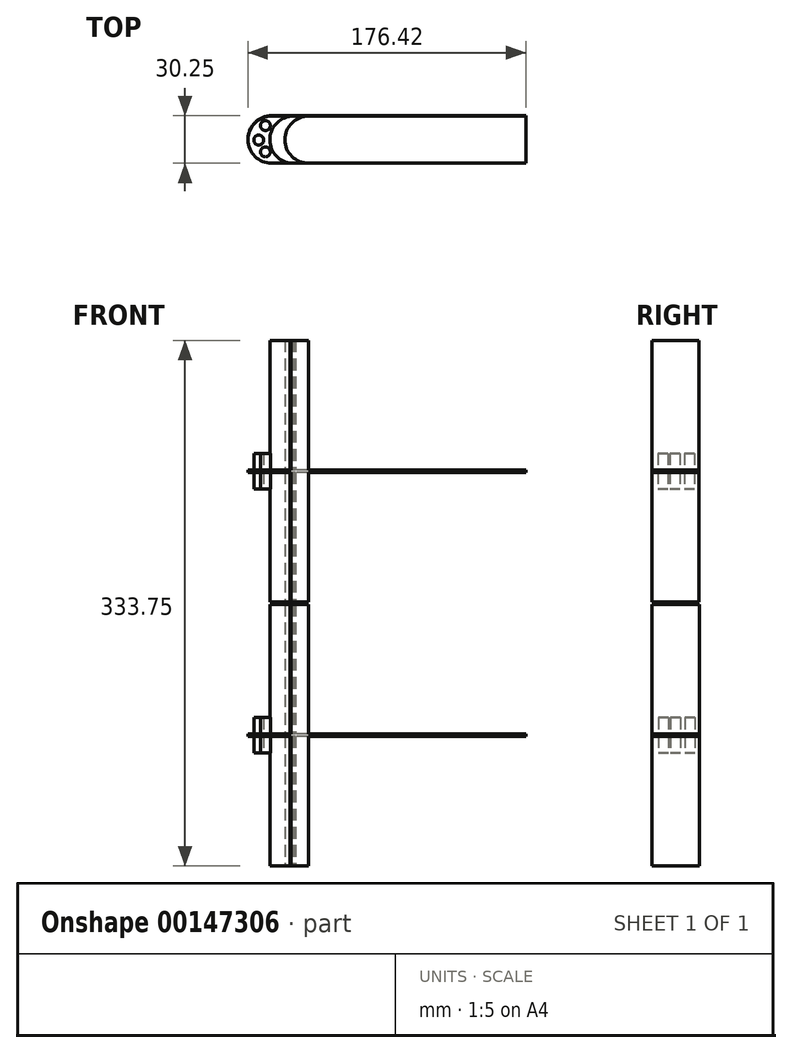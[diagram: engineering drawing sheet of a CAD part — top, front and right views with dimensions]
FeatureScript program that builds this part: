
annotation { "Feature Type Name" : "Feature", "Feature Type Description" : "" }
export const myFeature = defineFeature(function(context is Context, id is Id, definition is map)
    precondition{}
    {
        {
            var Q0;
            Q0=qCreatedBy(makeId("Top.planeOp"),FACE);
            var sketch = newSketch(context, id + "F0", { "sketchPlane" : qUnion([Q0])});
            skLineSegment(sketch, "E0.bottom", {"start": v(53.72, 4.42) * mm, "end": v(-107.7, 4.42) * mm});
            skLineSegment(sketch, "E0.top", {"start": v(53.72, 34.42) * mm, "end": v(-107.7, 34.42) * mm});
            skLineSegment(sketch, "E0.left", {"start": v(53.72, 4.42) * mm, "end": v(53.72, 34.42) * mm});
            skArc(sketch, "E1", {"start": v(-107.7, 34.42) * mm, "mid": v(-122.7, 19.42) * mm, "end": v(-107.7, 4.42) * mm});
            skCircle(sketch, "E2", {"center": v(-111.67, 28.37) * mm, "radius": 3.14 * mm});
            skCircle(sketch, "E3", {"center": v(-115.9, 19.19) * mm, "radius": 3.14 * mm});
            skCircle(sketch, "E4", {"center": v(-111.67, 11.65) * mm, "radius": 3.14 * mm});
            skArc(sketch, "E5", {"start": v(-93.88, 34.3) * mm, "mid": v(-108.84, 20.42) * mm, "end": v(-96.1, 4.47) * mm});
            skArc(sketch, "E6", {"start": v(-84.27, 34.42) * mm, "mid": v(-99.27, 19.42) * mm, "end": v(-84.27, 4.42) * mm});
            skLineSegment(sketch, "E7", {"start": v(-93.88, 34.3) * mm, "end": v(-92.5, 34.42) * mm});
            skLineSegment(sketch, "E8", {"start": v(-96.1, 4.47) * mm, "end": v(-95.4, 4.42) * mm});
            skSolve(sketch);
        }
        {
            var Q0;
            Q0 = qSketchRegion(id + "F0", true);
            extrude(context, id + "F1", {"entities" : qUnion([Q0]), "endBound" : BoundingType.SYMMETRIC, "depth" : 1.5 * mm});
        }
        {
            var Q0;
            Q0=makeQuery(id+"F0.imprint","IMPRINT",FACE,{"disambiguationData":[TD([[makeQuery(id+"F0.imprint","IMPRINT",EDGE,{"derivedFrom":sQuery(id+"F0.wireOp",EDGE,"E5")}),1.0]])]});
            extrude(context, id + "F2", {"entities" : qUnion([Q0]), "operationType" : NewBodyOperationType.ADD, "endBound" : BoundingType.SYMMETRIC, "depth" : 166 * mm});
        }
        {
            var Q0;
            Q0=makeQuery(id+"F0.imprint","IMPRINT",FACE,{"disambiguationData":[TD([[makeQuery(id+"F0.imprint","IMPRINT",EDGE,{"derivedFrom":sQuery(id+"F0.wireOp",EDGE,"E2")}),1.0]])]});
            var Q1;
            Q1=makeQuery(id+"F0.imprint","IMPRINT",FACE,{"disambiguationData":[TD([[makeQuery(id+"F0.imprint","IMPRINT",EDGE,{"derivedFrom":sQuery(id+"F0.wireOp",EDGE,"E3")}),1.0]])]});
            var Q2;
            Q2=makeQuery(id+"F0.imprint","IMPRINT",FACE,{"disambiguationData":[TD([[makeQuery(id+"F0.imprint","IMPRINT",EDGE,{"derivedFrom":sQuery(id+"F0.wireOp",EDGE,"E4")}),1.0]])]});
            extrude(context, id + "F3", {"entities" : qUnion([Q0, Q1, Q2]), "operationType" : NewBodyOperationType.ADD, "endBound" : BoundingType.SYMMETRIC, "depth" : 22.5 * mm});
        }
        {
            var Q0;
            Q0=makeQuery(id+"F1.opExtrude","SWEPT_BODY",BODY,{"disambiguationData":[OSD([sQuery(id+"F0.wireOp",EDGE,"E0.bottom"),sQuery(id+"F0.wireOp",EDGE,"E0.top"),sQuery(id+"F0.wireOp",EDGE,"E0.left"),sQuery(id+"F0.wireOp",EDGE,"E1"),sQuery(id+"F0.wireOp",EDGE,"E2"),sQuery(id+"F0.wireOp",EDGE,"E3"),sQuery(id+"F0.wireOp",EDGE,"E4")])]});
            transform(context, id + "F4", {"entities" : qUnion([Q0]), "transformType" : TransformType.TRANSLATION_3D, "dx" : 0 * mm, "dy" : -0.25 * mm, "dz" : 167.75 * mm, "makeCopy" : true});
        }
    });
